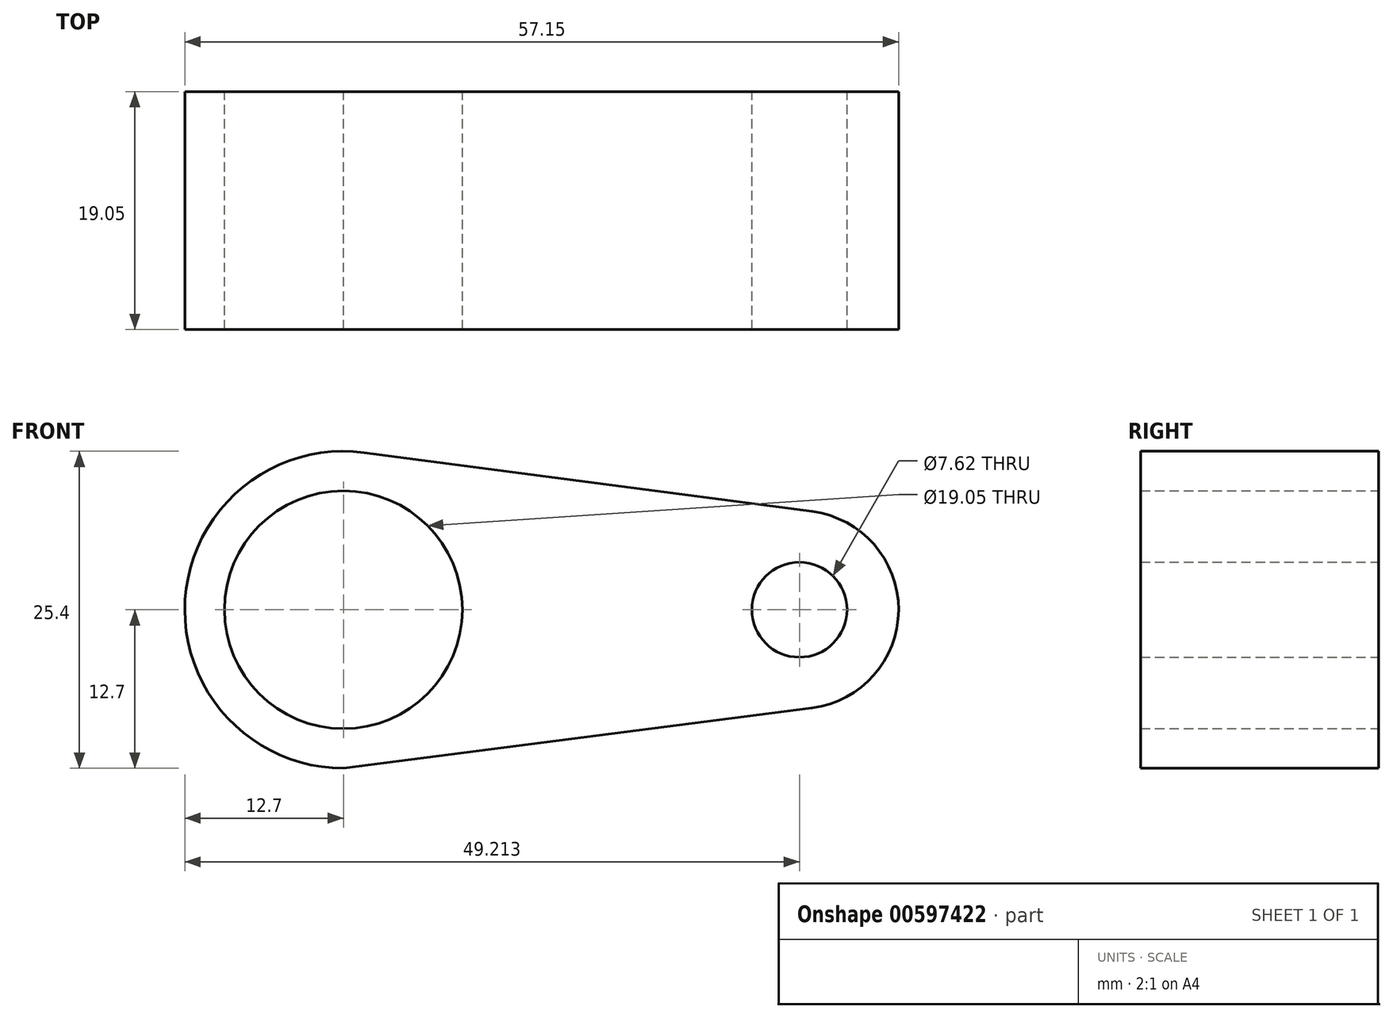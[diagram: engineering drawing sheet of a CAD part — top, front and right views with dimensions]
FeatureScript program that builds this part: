
annotation { "Feature Type Name" : "Feature", "Feature Type Description" : "" }
export const myFeature = defineFeature(function(context is Context, id is Id, definition is map)
    precondition{}
    {
        {
            var Q0;
            Q0=qCreatedBy(makeId("Front.planeOp"),FACE);
            var sketch = newSketch(context, id + "F0", { "sketchPlane" : qUnion([Q0])});
            skCircle(sketch, "E0", {"center": v(0, 0) * mm, "radius": 12.7 * mm});
            skCircle(sketch, "E1", {"center": v(36.51, 0) * mm, "radius": 7.94 * mm});
            skLineSegment(sketch, "E2", {"start": v(0, -12.7) * mm, "end": v(37.53, -7.87) * mm});
            skLineSegment(sketch, "E3", {"start": v(1.66, 12.6) * mm, "end": v(37.55, 7.87) * mm});
            skCircle(sketch, "E4", {"center": v(0, 0) * mm, "radius": 9.53 * mm});
            skCircle(sketch, "E5", {"center": v(36.51, 0) * mm, "radius": 3.81 * mm});
            skSolve(sketch);
        }
        {
            var Q0;
            {var subQ0=sQuery(id+"F0.wireOp",EDGE,"E3");Q0=makeQuery(id+"F0.imprint","IMPRINT",FACE,{"disambiguationData":[TD([[makeQuery(id+"F0.imprint","IMPRINT",EDGE,{"derivedFrom":subQ0}),-1.0]])]});}
            var Q1;
            Q1=makeQuery(id+"F0.imprint","IMPRINT",FACE,{"disambiguationData":[TD([[makeQuery(id+"F0.imprint","IMPRINT",EDGE,{"derivedFrom":sQuery(id+"F0.wireOp",EDGE,"E5")}),-1.0]])]});
            var Q2;
            Q2=makeQuery(id+"F0.imprint","IMPRINT",FACE,{"disambiguationData":[TD([[makeQuery(id+"F0.imprint","IMPRINT",EDGE,{"derivedFrom":sQuery(id+"F0.wireOp",EDGE,"E4")}),-1.0]])]});
            extrude(context, id + "F1", {"entities" : qUnion([Q0, Q1, Q2]), "depth" : 19.05 * mm, "offsetDistance" : 25.4 * mm});
        }
    });
